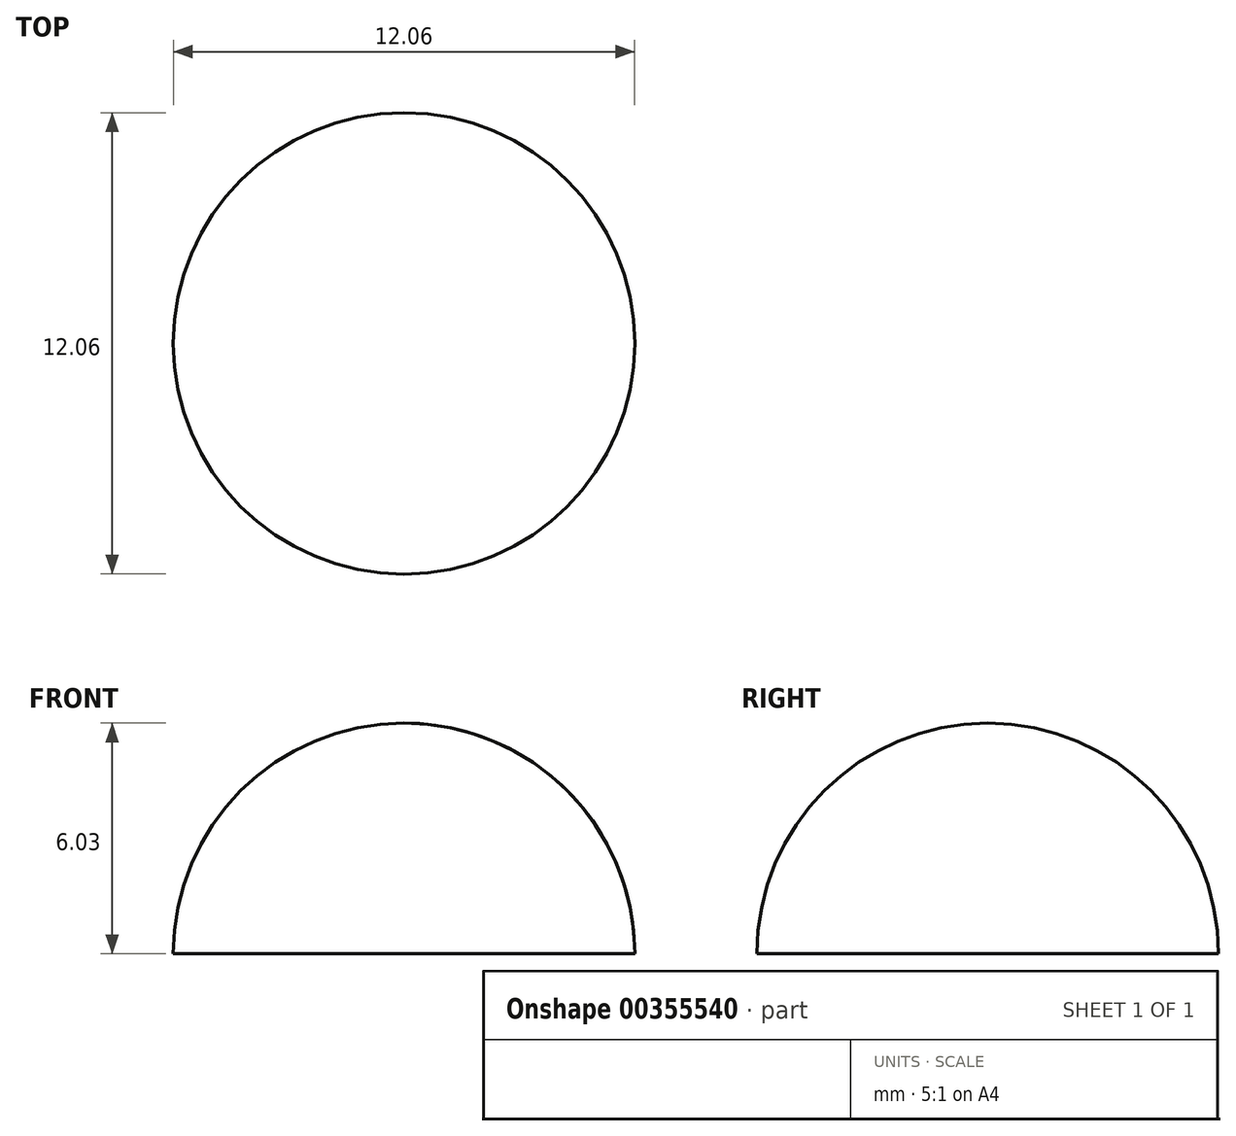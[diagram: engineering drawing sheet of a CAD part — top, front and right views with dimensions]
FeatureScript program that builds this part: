
annotation { "Feature Type Name" : "Feature", "Feature Type Description" : "" }
export const myFeature = defineFeature(function(context is Context, id is Id, definition is map)
    precondition{}
    {
        {
            var Q0;
            Q0=qCreatedBy(makeId("Front.planeOp"),FACE);
            var sketch = newSketch(context, id + "F0", { "sketchPlane" : qUnion([Q0])});
            skArc(sketch, "E0", {"start": v(6.03, 0) * mm, "mid": v(4.27, 4.27) * mm, "end": v(0, 6.03) * mm});
            skLineSegment(sketch, "E1", {"start": v(0, 6.03) * mm, "end": v(0, 0) * mm});
            skLineSegment(sketch, "E2", {"start": v(6.03, 0) * mm, "end": v(0, 0) * mm});
            skSolve(sketch);
        }
        {
            var Q0;
            Q0=qCreatedBy(makeId("Front.planeOp"),FACE);
            var sketch = newSketch(context, id + "F1", { "sketchPlane" : qUnion([Q0])});
            skLineSegment(sketch, "E3", {"start": v(0, -25.99) * mm, "end": v(0, 29.57) * mm, "construction": true});
            skSolve(sketch);
        }
        {
            var Q0;
            Q0=makeQuery(id+"F0.imprint","IMPRINT",FACE,{"disambiguationData":[TD([[makeQuery(id+"F0.imprint","IMPRINT",EDGE,{"derivedFrom":sQuery(id+"F0.wireOp",EDGE,"E0")}),1.0]])]});
            var Q1;
            Q1=sQuery(id+"F1.wireOp",EDGE,"E3");
            revolve(context, id + "F2", {"entities" : qUnion([Q0]), "axis" : qUnion([Q1]), "revolveType" : RevolveType.FULL});
        }
    });
